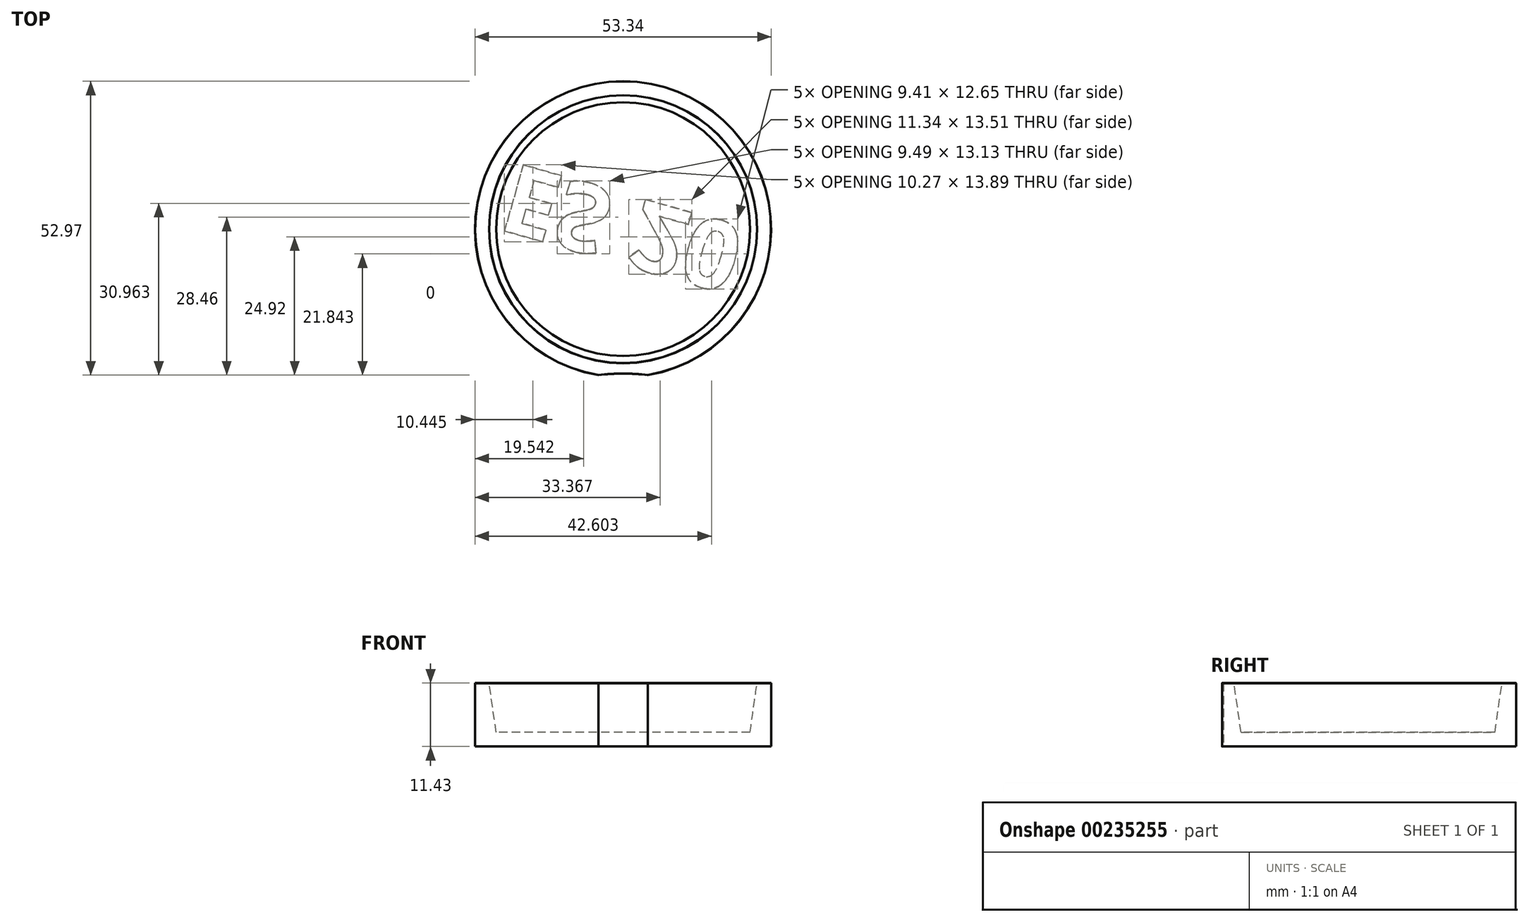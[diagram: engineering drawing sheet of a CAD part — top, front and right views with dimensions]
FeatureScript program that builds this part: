
annotation { "Feature Type Name" : "Feature", "Feature Type Description" : "" }
export const myFeature = defineFeature(function(context is Context, id is Id, definition is map)
    precondition{}
    {
        {
            assignVariable(context, id + "F0", {"name" : "SideThickness", "anyValue" : .1});
        }
        {
            assignVariable(context, id + "F1", {"name" : "TopThickness", "anyValue" : .1});
        }
        {
            var Q0;
            Q0=qCreatedBy(makeId("Front.planeOp"),FACE);
            var sketch = newSketch(context, id + "F2", { "sketchPlane" : qUnion([Q0])});
            skLineSegment(sketch, "E0", {"start": v(0, 0) * mm, "end": v(26.67, 0) * mm});
            skLineSegment(sketch, "E1", {"start": v(26.67, 0) * mm, "end": v(26.67, 11.43) * mm});
            skLineSegment(sketch, "E2", {"start": v(26.67, 11.43) * mm, "end": v(24.13, 11.43) * mm});
            skLineSegment(sketch, "E3", {"start": v(24.13, 11.43) * mm, "end": v(22.86, 2.54) * mm});
            skLineSegment(sketch, "E4", {"start": v(22.86, 2.54) * mm, "end": v(0, 2.54) * mm});
            skLineSegment(sketch, "E5", {"start": v(0, 2.54) * mm, "end": v(0, 0) * mm});
            skLineSegment(sketch, "E6", {"start": v(0, 10.55) * mm, "end": v(0, -12.08) * mm, "construction": true});
            skSolve(sketch);
        }
        {
            var Q0;
            Q0 = qSketchRegion(id + "F2", true);
            var Q1;
            Q1=sQuery(id+"F2.wireOp",EDGE,"E6");
            revolve(context, id + "F3", {"surfaceOperationType" : NewSurfaceOperationType.NEW, "entities" : qUnion([Q0]), "axis" : qUnion([Q1]), "revolveType" : RevolveType.FULL});
        }
        {
            var Q0;
            Q0=makeQuery(id+"F3.opRevolve","SWEPT_FACE",FACE,{"disambiguationData":[OSD([sQuery(id+"F2.wireOp",EDGE,"E0")])]});
            var sketch = newSketch(context, id + "F4", { "sketchPlane" : qUnion([Q0])});
            skText(sketch, "E7", { "text": "ES 20 ", "fontName": "OpenSans-Bold.ttf"});
            skCircle(sketch, "E8", {"center": v(0, 0) * mm, "radius": 22.86 * mm, "construction": true});
            const initialGuessF4  = {"E7": [-0.01946, -0.012, 0.96213, 0.27258, 0.01246]};
            skSetInitialGuess(sketch, initialGuessF4);
            skSolve(sketch);
        }
        {
            var Q0;
            Q0 = qSketchRegion(id + "F4", true);
            extrude(context, id + "F5", {"entities" : qUnion([Q0]), "operationType" : NewBodyOperationType.REMOVE, "oppositeDirection" : true, "depth" : (getVariable(context, 'TopThickness') / 2) * mm, "offsetDistance" : 25.4 * mm});
        }
        {
            var Q0;
            Q0=makeQuery(id+"F4.imprint","IMPRINT",FACE,{"disambiguationData":[TD([[makeQuery(id+"F4.imprint","IMPRINT",EDGE,{"derivedFrom":sQuery(id+"F4.wireOp",EDGE,"E7.sketch_text.stroke-0")}),1.0]])]});
            var sketch = newSketch(context, id + "F6", { "sketchPlane" : qUnion([Q0])});
            skCircle(sketch, "E9", {"center": v(0, 64.14) * mm, "radius": 38.1 * mm});
            skSolve(sketch);
        }
        {
            var Q0;
            Q0 = qSketchRegion(id + "F6", true);
            extrude(context, id + "F7", {"entities" : qUnion([Q0]), "operationType" : NewBodyOperationType.REMOVE, "endBound" : BoundingType.THROUGH_ALL, "oppositeDirection" : true, "depth" : 25.4 * mm, "offsetDistance" : 25.4 * mm});
        }
        {
            var Q0;
            Q0=makeQuery(id+"F5.boolean.opBoolean","SPLIT",FACE,{"disambiguationData":[TD([makeQuery(id+"F3.opRevolve","SWEPT_FACE",FACE,{"disambiguationData":[OSD([sQuery(id+"F2.wireOp",EDGE,"E1")])]})])],"derivedFrom":makeQuery(id+"F3.opRevolve","SWEPT_FACE",FACE,{"disambiguationData":[OSD([sQuery(id+"F2.wireOp",EDGE,"E0")])]})});
            chamfer(context, id + "F8", {"entities" : qUnion([Q0]), "width" : (getVariable(context, 'SideThickness') / 4) * mm, "tangentPropagation" : true});
        }
        {
            var Q0;
            Q0=makeQuery(id+"F3.opRevolve","SWEPT_FACE",FACE,{"disambiguationData":[OSD([sQuery(id+"F2.wireOp",EDGE,"E2")])]});
            chamfer(context, id + "F9", {"entities" : qUnion([Q0]), "width" : (getVariable(context, 'SideThickness') / 4) * mm, "tangentPropagation" : true});
        }
    });
